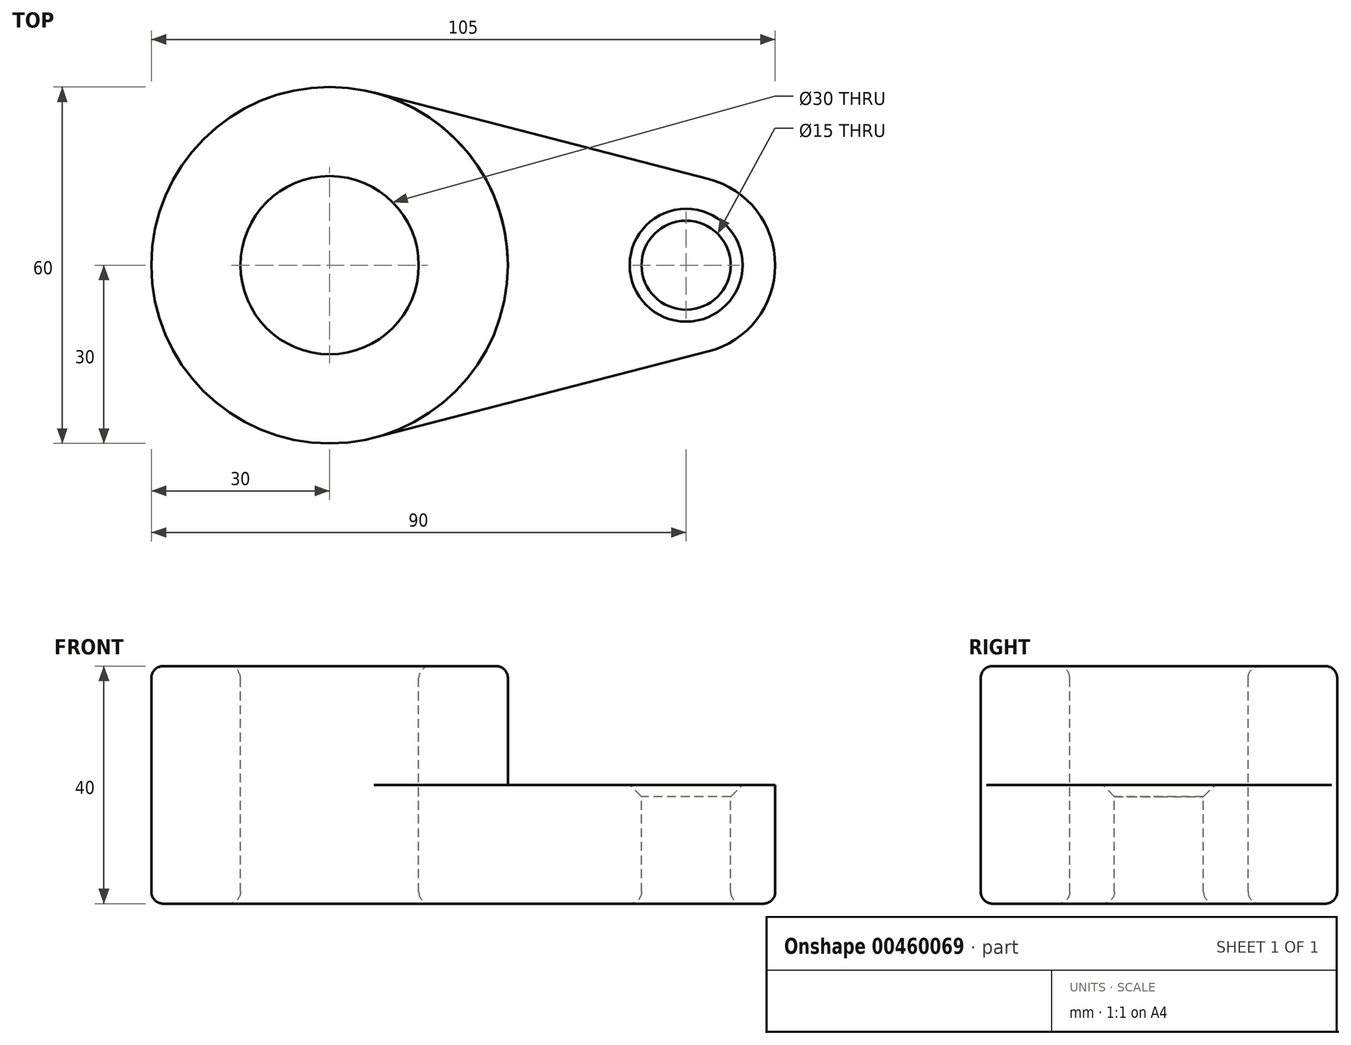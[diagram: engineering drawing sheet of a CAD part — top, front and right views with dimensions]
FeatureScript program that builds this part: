
annotation { "Feature Type Name" : "Feature", "Feature Type Description" : "" }
export const myFeature = defineFeature(function(context is Context, id is Id, definition is map)
    precondition{}
    {
        {
            var Q0;
            Q0=qCreatedBy(makeId("Top.planeOp"),FACE);
            var sketch = newSketch(context, id + "F0", { "sketchPlane" : qUnion([Q0])});
            skCircle(sketch, "E0", {"center": v(0, 0) * mm, "radius": 30 * mm});
            skCircle(sketch, "E1", {"center": v(60, 0) * mm, "radius": 15 * mm});
            skLineSegment(sketch, "E2", {"start": v(7.5, 29.05) * mm, "end": v(63.75, 14.52) * mm});
            skLineSegment(sketch, "E3", {"start": v(7.5, -29.05) * mm, "end": v(63.75, -14.52) * mm});
            skCircle(sketch, "E4", {"center": v(0, 0) * mm, "radius": 15 * mm});
            skCircle(sketch, "E5", {"center": v(60, 0) * mm, "radius": 7.5 * mm});
            skSolve(sketch);
        }
        {
            var Q0;
            Q0=makeQuery(id+"F0.imprint","IMPRINT",FACE,{"disambiguationData":[TD([[makeQuery(id+"F0.imprint","IMPRINT",EDGE,{"derivedFrom":sQuery(id+"F0.wireOp",EDGE,"E4")}),-1.0]])]});
            var Q1;
            {var subQ0=sQuery(id+"F0.wireOp",EDGE,"E2");Q1=makeQuery(id+"F0.imprint","IMPRINT",FACE,{"disambiguationData":[TD([[makeQuery(id+"F0.imprint","IMPRINT",EDGE,{"derivedFrom":subQ0}),-1.0]])]});}
            var Q2;
            Q2=makeQuery(id+"F0.imprint","IMPRINT",FACE,{"disambiguationData":[TD([[makeQuery(id+"F0.imprint","IMPRINT",EDGE,{"derivedFrom":sQuery(id+"F0.wireOp",EDGE,"E5")}),-1.0]])]});
            extrude(context, id + "F1", {"entities" : qUnion([Q0, Q1, Q2]), "oppositeDirection" : true, "depth" : 20 * mm});
        }
        {
            var Q0;
            Q0=makeQuery(id+"F0.imprint","IMPRINT",FACE,{"disambiguationData":[TD([[makeQuery(id+"F0.imprint","IMPRINT",EDGE,{"derivedFrom":sQuery(id+"F0.wireOp",EDGE,"E4")}),-1.0]])]});
            extrude(context, id + "F2", {"entities" : qUnion([Q0]), "operationType" : NewBodyOperationType.ADD, "depth" : 20 * mm});
        }
        {
            var Q0;
            Q0=makeQuery(id+"F2.opExtrude","CAP_EDGE",EDGE,{"disambiguationData":[OSD([sQuery(id+"F0.wireOp",EDGE,"E0")])],"isStart":false});
            var Q1;
            Q1=makeQuery(id+"F2.opExtrude","CAP_EDGE",EDGE,{"disambiguationData":[OSD([sQuery(id+"F0.wireOp",EDGE,"E4")])],"isStart":false});
            var Q2;
            Q2=makeQuery(id+"F1.opExtrude","CAP_FACE",FACE,{"disambiguationData":[OSD([sQuery(id+"F0.wireOp",EDGE,"E0"),sQuery(id+"F0.wireOp",EDGE,"E1"),sQuery(id+"F0.wireOp",EDGE,"E2"),sQuery(id+"F0.wireOp",EDGE,"E3"),sQuery(id+"F0.wireOp",EDGE,"E4"),sQuery(id+"F0.wireOp",EDGE,"E5")])],"isStart":false});
            fillet(context, id + "F3", {"entities" : qUnion([Q0, Q1, Q2]), "radius" : 2 * mm, "tangentPropagation" : true, "allowEdgeOverflow" : false});
        }
        {
            var Q0;
            Q0=makeQuery(id+"F1.opExtrude","CAP_EDGE",EDGE,{"disambiguationData":[OSD([sQuery(id+"F0.wireOp",EDGE,"E5")])],"isStart":true});
            chamfer(context, id + "F4", {"entities" : qUnion([Q0]), "width" : 2 * mm, "tangentPropagation" : true});
        }
    });
